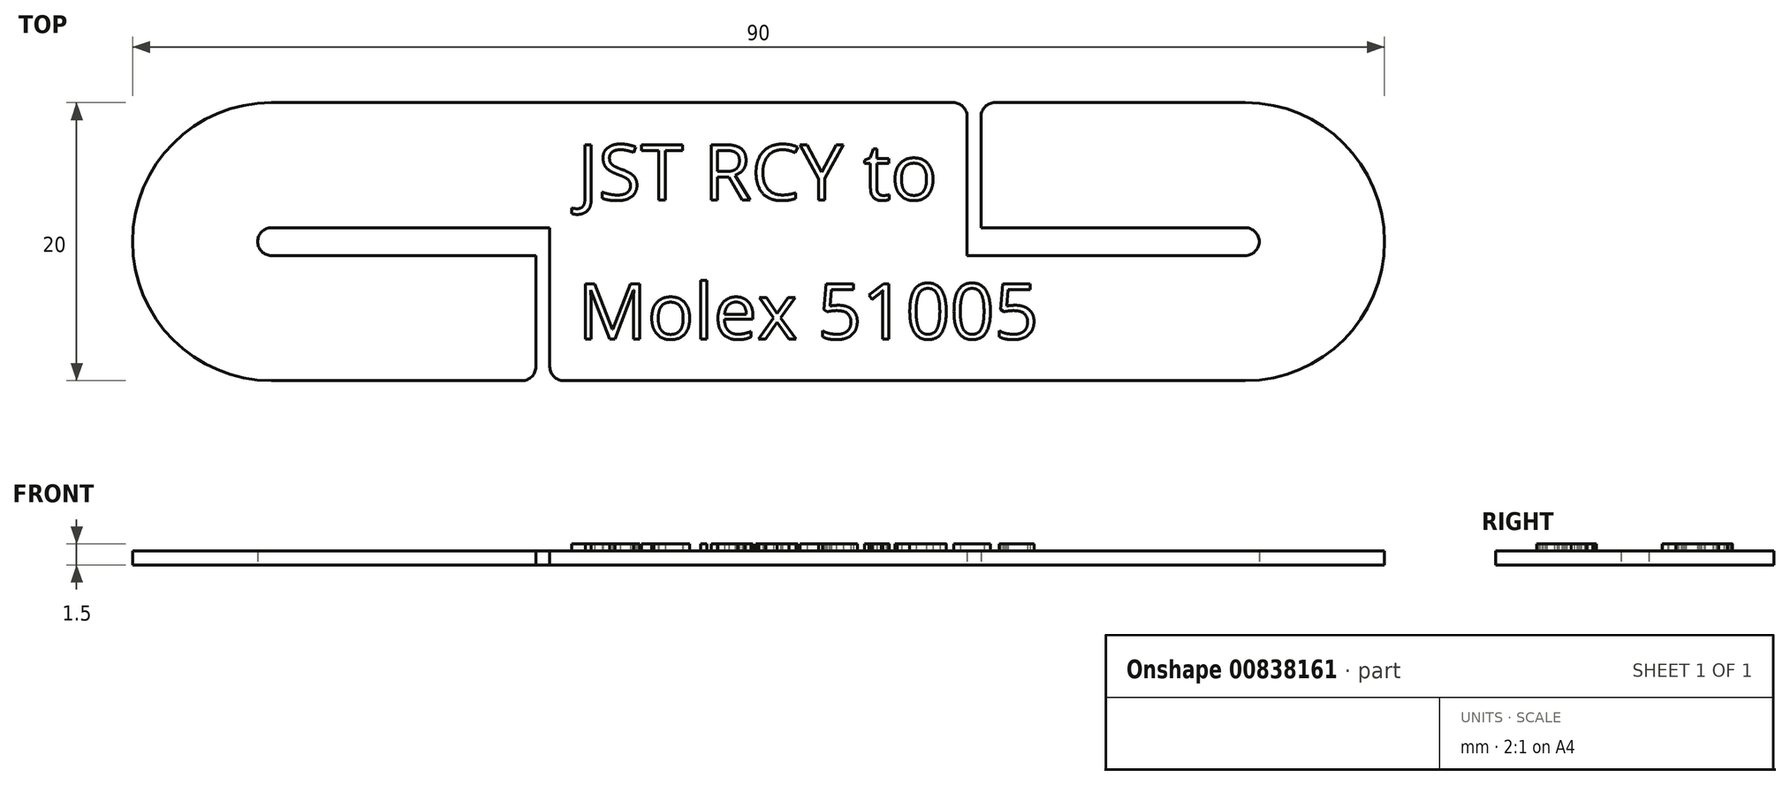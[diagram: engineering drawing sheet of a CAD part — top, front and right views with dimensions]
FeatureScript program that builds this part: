
annotation { "Feature Type Name" : "Feature", "Feature Type Description" : "" }
export const myFeature = defineFeature(function(context is Context, id is Id, definition is map)
    precondition{}
    {
        {
            var Q0;
            Q0=qCreatedBy(makeId("Top.planeOp"),FACE);
            var sketch = newSketch(context, id + "F0", { "sketchPlane" : qUnion([Q0])});
            skLineSegment(sketch, "E0.bottom", {"start": v(-15, 10) * mm, "end": v(14, 10) * mm});
            skLineSegment(sketch, "E0.top", {"start": v(-14, -10) * mm, "end": v(15, -10) * mm});
            skLineSegment(sketch, "E0.left", {"start": v(-15, 10) * mm, "end": v(-15, -9) * mm});
            skLineSegment(sketch, "E0.right", {"start": v(15, 9) * mm, "end": v(15, -10) * mm});
            skPoint(sketch, "E0.middle", {"position": v(0, 0) * mm});
            skLineSegment(sketch, "E1.bottom", {"start": v(-15, 10) * mm, "end": v(-35, 10) * mm});
            skLineSegment(sketch, "E1.top", {"start": v(-15, 1) * mm, "end": v(-35, 1) * mm});
            skLineSegment(sketch, "E1.left", {"start": v(-15, 10) * mm, "end": v(-15, 1) * mm, "construction": true});
            skLineSegment(sketch, "E1.right", {"start": v(-35, 10) * mm, "end": v(-35, 1) * mm, "construction": true});
            skLineSegment(sketch, "E2.bottom", {"start": v(-35, -1) * mm, "end": v(-16, -1) * mm});
            skLineSegment(sketch, "E2.top", {"start": v(-35, -10) * mm, "end": v(-17, -10) * mm});
            skLineSegment(sketch, "E2.left", {"start": v(-35, -1) * mm, "end": v(-35, -10) * mm, "construction": true});
            skLineSegment(sketch, "E2.right", {"start": v(-16, -1) * mm, "end": v(-16, -9) * mm});
            skLineSegment(sketch, "E3", {"start": v(-35, 1) * mm, "end": v(-35, -1) * mm, "construction": true});
            skPoint(sketch, "E4", {"position": v(-35, 0) * mm});
            skArc(sketch, "E5", {"start": v(-35, 10) * mm, "mid": v(-45, 0) * mm, "end": v(-35, -10) * mm});
            skArc(sketch, "E6", {"start": v(-35, 1) * mm, "mid": v(-36, 0) * mm, "end": v(-35, -1) * mm});
            skLineSegment(sketch, "E7.bottom", {"start": v(15, -10) * mm, "end": v(35, -10) * mm});
            skLineSegment(sketch, "E7.top", {"start": v(15, -1) * mm, "end": v(35, -1) * mm});
            skLineSegment(sketch, "E7.left", {"start": v(15, -10) * mm, "end": v(15, -1) * mm, "construction": true});
            skLineSegment(sketch, "E7.right", {"start": v(35, -10) * mm, "end": v(35, -1) * mm, "construction": true});
            skLineSegment(sketch, "E8.bottom", {"start": v(35, 1) * mm, "end": v(16, 1) * mm});
            skLineSegment(sketch, "E8.top", {"start": v(35, 10) * mm, "end": v(17, 10) * mm});
            skLineSegment(sketch, "E8.left", {"start": v(35, 1) * mm, "end": v(35, 10) * mm, "construction": true});
            skLineSegment(sketch, "E8.right", {"start": v(16, 1) * mm, "end": v(16, 9) * mm});
            skLineSegment(sketch, "E9", {"start": v(35, 1) * mm, "end": v(35, -1) * mm, "construction": true});
            skPoint(sketch, "E10", {"position": v(35, 0) * mm});
            skArc(sketch, "E11.MirrorCS", {"start": v(35, 1) * mm, "mid": v(36, 0) * mm, "end": v(35, -1) * mm});
            skArc(sketch, "E12.MirrorCS", {"start": v(35, 10) * mm, "mid": v(45, 0) * mm, "end": v(35, -10) * mm});
            skPoint(sketch, "E13.visualSharp", {"position": v(16, 10) * mm});
            skArc(sketch, "E13.filletArc", {"start": v(17, 10) * mm, "mid": v(16.3, 9.7) * mm, "end": v(16, 9) * mm});
            skPoint(sketch, "E14.visualSharp", {"position": v(15, 10) * mm});
            skArc(sketch, "E14.filletArc", {"start": v(15, 9) * mm, "mid": v(14.7, 9.7) * mm, "end": v(14, 10) * mm});
            skPoint(sketch, "E15.visualSharp", {"position": v(-16, -10) * mm});
            skArc(sketch, "E15.filletArc", {"start": v(-17, -10) * mm, "mid": v(-16.3, -9.7) * mm, "end": v(-16, -9) * mm});
            skPoint(sketch, "E16.visualSharp", {"position": v(-15, -10) * mm});
            skArc(sketch, "E16.filletArc", {"start": v(-15, -9) * mm, "mid": v(-14.7, -9.7) * mm, "end": v(-14, -10) * mm});
            skSolve(sketch);
        }
        {
            var Q0;
            {var subQ1=sQuery(id+"F0.wireOp",EDGE,"E0.bottom");Q0=makeQuery(id+"F0.imprint","IMPRINT",FACE,{"disambiguationData":[TD([[makeQuery(id+"F0.imprint","IMPRINT",EDGE,{"derivedFrom":subQ1}),-1.0]])]});}
            var Q1;
            {var subQ1=sQuery(id+"F0.wireOp",EDGE,"E1.bottom");Q1=makeQuery(id+"F0.imprint","IMPRINT",FACE,{"disambiguationData":[TD([[makeQuery(id+"F0.imprint","IMPRINT",EDGE,{"derivedFrom":subQ1}),1.0]])]});}
            var Q2;
            {var subQ1=sQuery(id+"F0.wireOp",EDGE,"E7.bottom");Q2=makeQuery(id+"F0.imprint","IMPRINT",FACE,{"disambiguationData":[TD([[makeQuery(id+"F0.imprint","IMPRINT",EDGE,{"derivedFrom":subQ1}),1.0]])]});}
            extrude(context, id + "F1", {"entities" : qUnion([Q0, Q1, Q2]), "depth" : 1 * mm, "offsetDistance" : 25 * mm});
        }
        {
            var Q0;
            Q0=makeQuery(id+"F1.opExtrude","CAP_FACE",FACE,{"disambiguationData":[OSD([sQuery(id+"F0.wireOp",EDGE,"E0.bottom"),sQuery(id+"F0.wireOp",EDGE,"E0.top"),sQuery(id+"F0.wireOp",EDGE,"E0.left"),sQuery(id+"F0.wireOp",EDGE,"E0.right"),sQuery(id+"F0.wireOp",EDGE,"E1.bottom"),sQuery(id+"F0.wireOp",EDGE,"E1.top"),sQuery(id+"F0.wireOp",EDGE,"E2.bottom"),sQuery(id+"F0.wireOp",EDGE,"E2.top"),sQuery(id+"F0.wireOp",EDGE,"E2.right"),sQuery(id+"F0.wireOp",EDGE,"E5"),sQuery(id+"F0.wireOp",EDGE,"E6"),sQuery(id+"F0.wireOp",EDGE,"E7.bottom"),sQuery(id+"F0.wireOp",EDGE,"E7.top"),sQuery(id+"F0.wireOp",EDGE,"E8.bottom"),sQuery(id+"F0.wireOp",EDGE,"E8.top"),sQuery(id+"F0.wireOp",EDGE,"E8.right"),sQuery(id+"F0.wireOp",EDGE,"E11.MirrorCS"),sQuery(id+"F0.wireOp",EDGE,"E12.MirrorCS")])],"isStart":false});
            var sketch = newSketch(context, id + "F2", { "sketchPlane" : qUnion([Q0])});
            skText(sketch, "E17", { "text": "JST RCY to", "fontName": "OpenSans-Regular.ttf"});
            skText(sketch, "E18", { "text": "Molex 51005", "fontName": "OpenSans-Regular.ttf"});
            const initialGuessF2  = {"E17": [-0.013, 0.003, 1, 0, 0.004], "E18": [-0.013, -0.007, 1, 0, 0.004]};
            skSetInitialGuess(sketch, initialGuessF2);
            skSolve(sketch);
        }
        {
            var Q0;
            Q0=makeQuery(id+"F2.imprint","IMPRINT",FACE,{"disambiguationData":[TD([[makeQuery(id+"F2.imprint","IMPRINT",EDGE,{"derivedFrom":sQuery(id+"F2.wireOp",EDGE,"E17.sketch_text.stroke-0")}),-1.0]])]});
            var Q1;
            Q1=makeQuery(id+"F2.imprint","IMPRINT",FACE,{"disambiguationData":[TD([[makeQuery(id+"F2.imprint","IMPRINT",EDGE,{"derivedFrom":sQuery(id+"F2.wireOp",EDGE,"E17.sketch_text.stroke-10")}),-1.0]])]});
            var Q2;
            Q2=makeQuery(id+"F2.imprint","IMPRINT",FACE,{"disambiguationData":[TD([[makeQuery(id+"F2.imprint","IMPRINT",EDGE,{"derivedFrom":sQuery(id+"F2.wireOp",EDGE,"E17.sketch_text.stroke-35")}),-1.0]])]});
            var Q3;
            Q3 = qSketchRegion(id + "F2", true);
            extrude(context, id + "F3", {"entities" : qUnion([Q0, Q1, Q2, Q3]), "operationType" : NewBodyOperationType.ADD, "depth" : 0.5 * mm, "offsetDistance" : 25 * mm});
        }
    });
